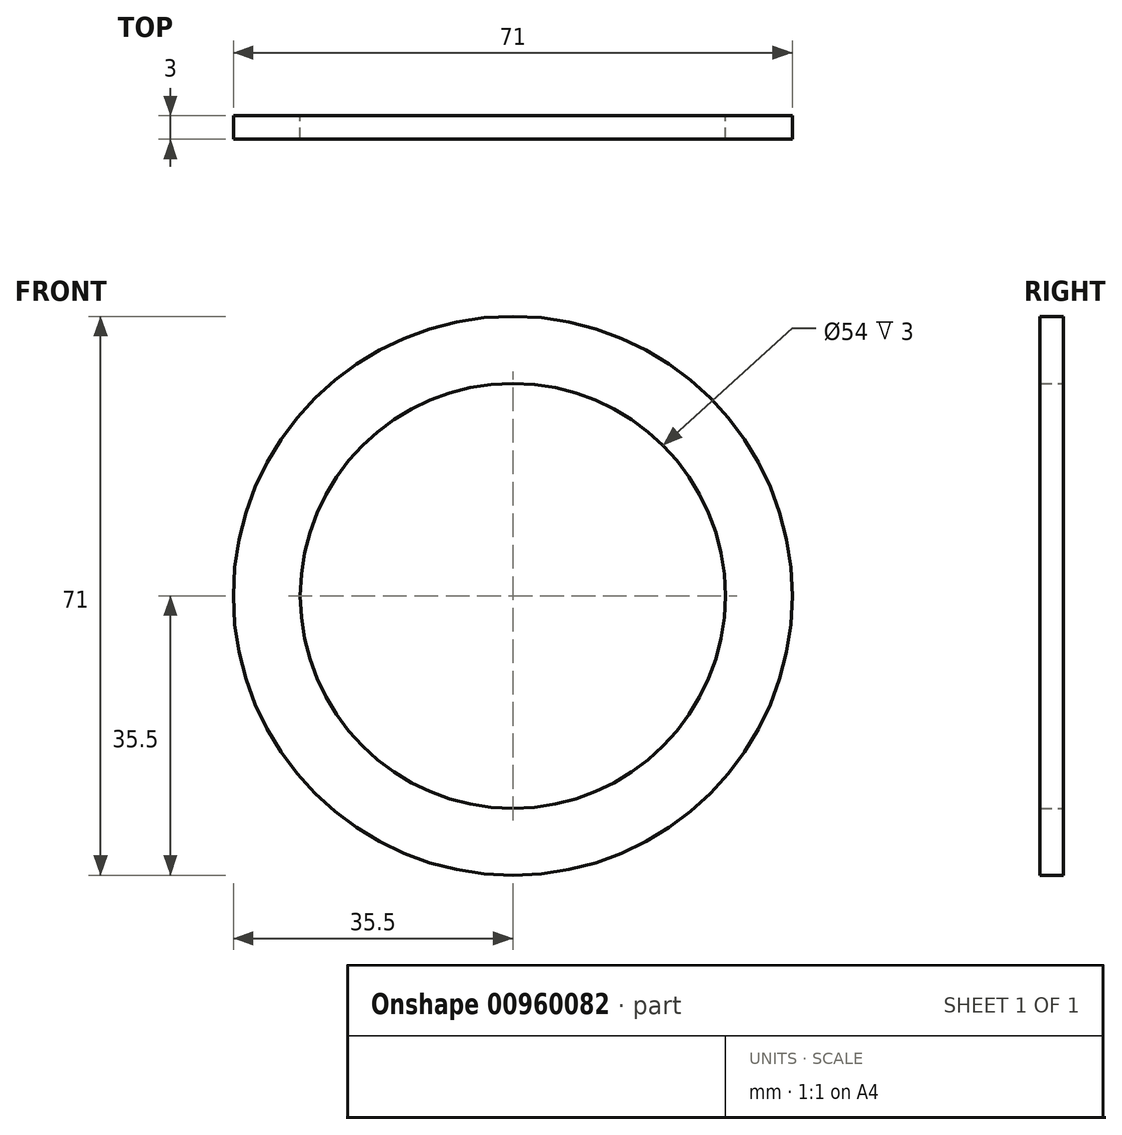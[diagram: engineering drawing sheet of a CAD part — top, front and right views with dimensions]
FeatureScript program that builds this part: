
annotation { "Feature Type Name" : "Feature", "Feature Type Description" : "" }
export const myFeature = defineFeature(function(context is Context, id is Id, definition is map)
    precondition{}
    {
        {
            var Q0;
            Q0=qCreatedBy(makeId("Front.planeOp"),FACE);
            var sketch = newSketch(context, id + "F0", { "sketchPlane" : qUnion([Q0])});
            skCircle(sketch, "E0", {"center": v(0, 0) * mm, "radius": 27 * mm});
            skCircle(sketch, "E1", {"center": v(0, 0) * mm, "radius": 35.5 * mm});
            skSolve(sketch);
        }
        {
            var Q0;
            Q0=makeQuery(id+"F0.imprint","IMPRINT",FACE,{"disambiguationData":[TD([[makeQuery(id+"F0.imprint","IMPRINT",EDGE,{"derivedFrom":sQuery(id+"F0.wireOp",EDGE,"E0")}),-1.0]])]});
            extrude(context, id + "F1", {"entities" : qUnion([Q0]), "depth" : 3 * mm, "offsetDistance" : 25 * mm});
        }
    });
